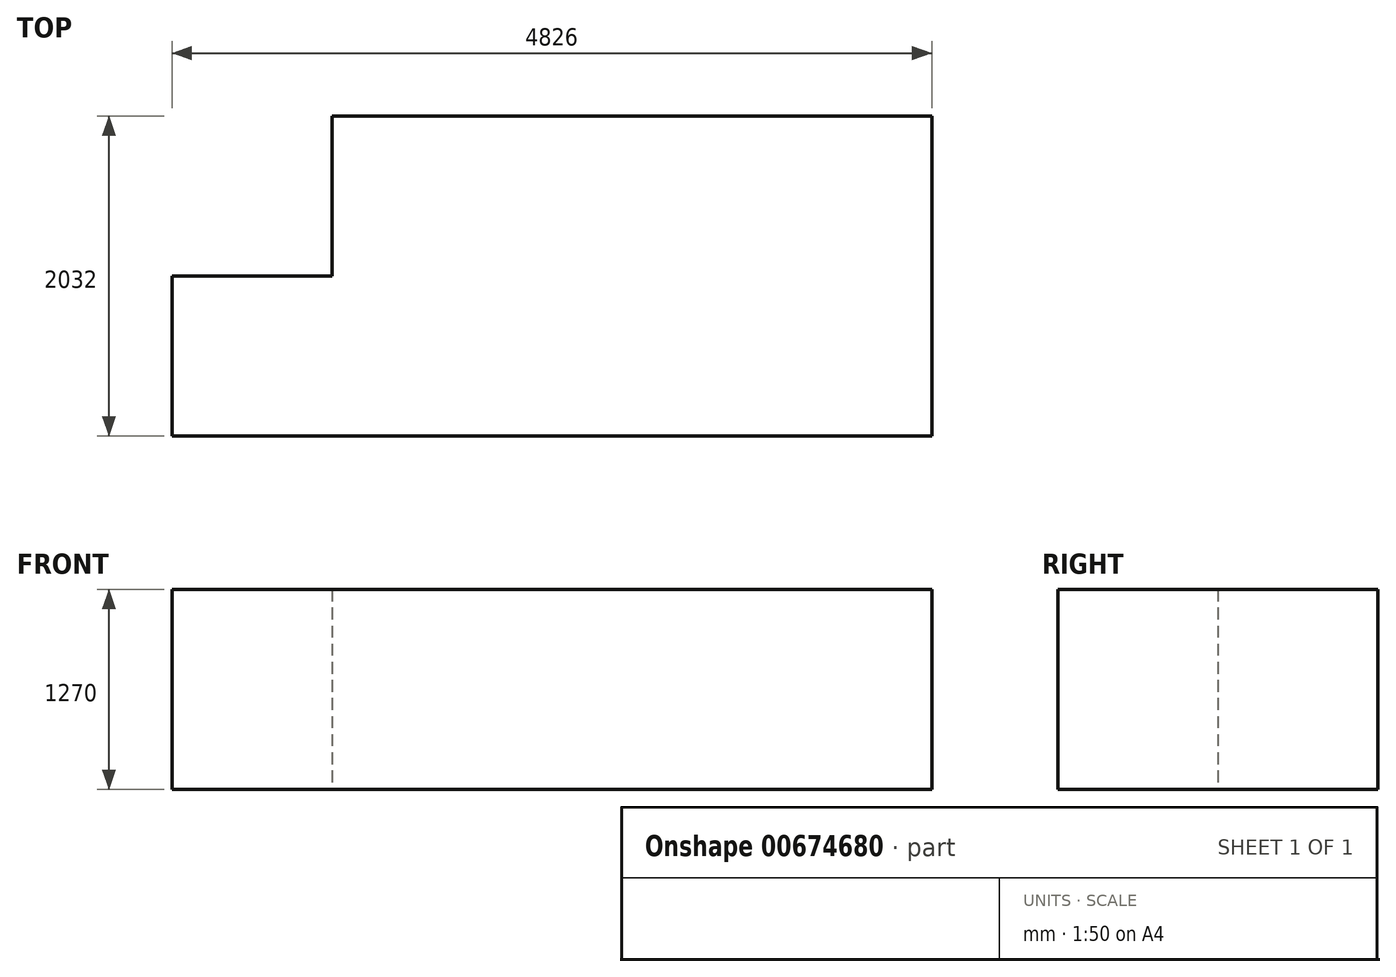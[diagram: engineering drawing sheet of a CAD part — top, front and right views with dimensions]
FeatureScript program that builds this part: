
annotation { "Feature Type Name" : "Feature", "Feature Type Description" : "" }
export const myFeature = defineFeature(function(context is Context, id is Id, definition is map)
    precondition{}
    {
        {
            var Q0;
            Q0=qCreatedBy(makeId("Top.planeOp"),FACE);
            var sketch = newSketch(context, id + "F0", { "sketchPlane" : qUnion([Q0])});
            skLineSegment(sketch, "E0.bottom", {"start": v(0, 0) * mm, "end": v(3810, 0) * mm});
            skLineSegment(sketch, "E0.top", {"start": v(0, 2032) * mm, "end": v(3810, 2032) * mm});
            skLineSegment(sketch, "E0.left", {"start": v(0, 0) * mm, "end": v(0, 2032) * mm});
            skLineSegment(sketch, "E0.right", {"start": v(3810, 0) * mm, "end": v(3810, 2032) * mm});
            skLineSegment(sketch, "E1.bottom", {"start": v(0, 0) * mm, "end": v(-1016, 0) * mm});
            skLineSegment(sketch, "E1.top", {"start": v(0, 1016) * mm, "end": v(-1016, 1016) * mm});
            skLineSegment(sketch, "E1.left", {"start": v(0, 0) * mm, "end": v(0, 1016) * mm});
            skLineSegment(sketch, "E1.right", {"start": v(-1016, 0) * mm, "end": v(-1016, 1016) * mm});
            skSolve(sketch);
        }
        {
            var Q0;
            Q0=makeQuery(id+"F0.imprint","IMPRINT",FACE,{"disambiguationData":[TD([[makeQuery(id+"F0.imprint","IMPRINT",EDGE,{"derivedFrom":sQuery(id+"F0.wireOp",EDGE,"E1.bottom")}),-1.0]])]});
            var Q1;
            Q1=makeQuery(id+"F0.imprint","IMPRINT",FACE,{"disambiguationData":[TD([[makeQuery(id+"F0.imprint","IMPRINT",EDGE,{"derivedFrom":sQuery(id+"F0.wireOp",EDGE,"E0.bottom")}),1.0]])]});
            extrude(context, id + "F1", {"entities" : qUnion([Q0, Q1]), "depth" : 1270 * mm, "offsetDistance" : 25.4 * mm});
        }
    });
